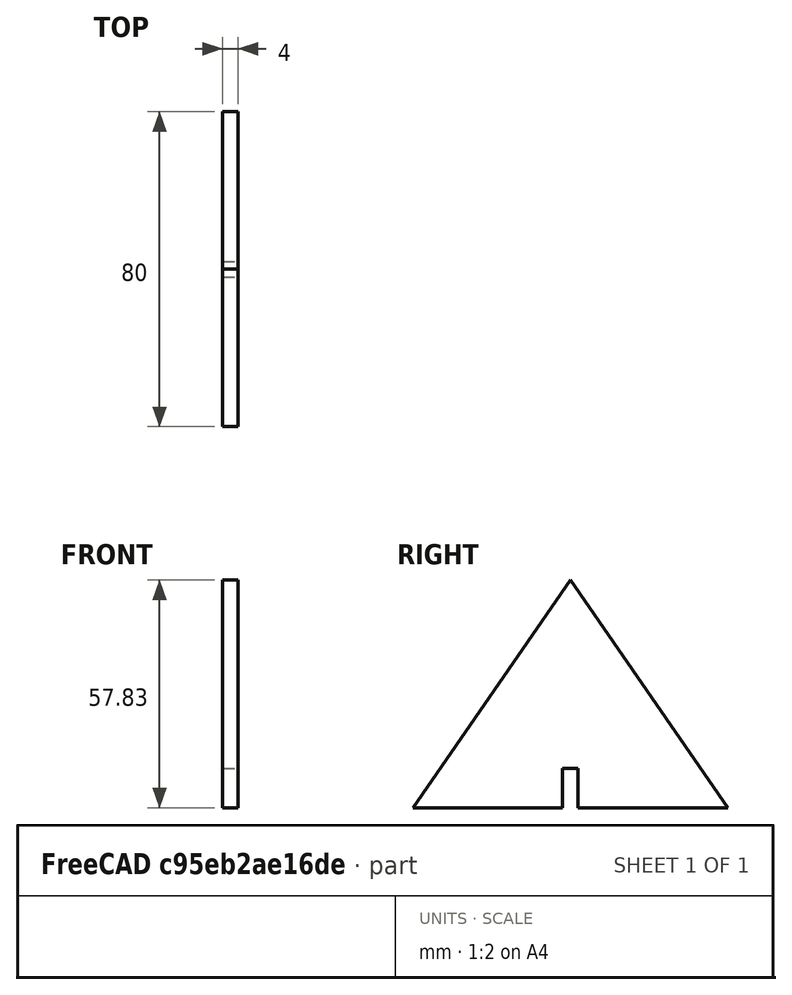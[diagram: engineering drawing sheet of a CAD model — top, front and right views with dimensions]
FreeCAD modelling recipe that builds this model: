
FCSTD DOCUMENT  (FreeCAD 0.18R16131 (Git))
Label: freccia
License: All rights reserved
LicenseURL: http://en.wikipedia.org/wiki/All_rights_reserved
objects: Sketcher::SketchObject×1, PartDesign::Pad×1, PartDesign::Body×1
note: 4 computed .brp shape members not serialized (recipe doc carries the construction recipe); baked Part::Feature solids carry a one-line shape summary decoded from their .brp

FEATURE [Sketcher::SketchObject] Sketch
  MapMode = 5
  Placement = pos=(0,0,0) rot=(0.57735,0.57735,0.57735;2.0944rad)
  Support = -> [YZ_Plane]
  sketch-geometry (7):
    g0: LineSegment StartX=0 StartY=58 StartZ=0 EndX=-40 EndY=0.173901 EndZ=0
    g1: LineSegment StartX=-40 StartY=0.173901 StartZ=0 EndX=-2 EndY=0.173901 EndZ=0
    g2: LineSegment StartX=40 StartY=0.173901 StartZ=0 EndX=0 EndY=58 EndZ=0
    g3: LineSegment StartX=2 StartY=0.173901 StartZ=0 EndX=2 EndY=10.1739 EndZ=0
    g4: LineSegment StartX=2 StartY=10.1739 StartZ=0 EndX=-2 EndY=10.1739 EndZ=0
    g5: LineSegment StartX=-2 StartY=10.1739 StartZ=0 EndX=-2 EndY=0.173901 EndZ=0
    g6: LineSegment StartX=2 StartY=0.173901 StartZ=0 EndX=40 EndY=0.173901 EndZ=0
  constraints (16):
    c: PointOnObject(g0,g-2)
    c: Coincident(g0,g1)
    c: Coincident(g6,g2)
    c: Coincident(g2,g0)
    c: Symmetric(g6,g0,g-2)
    c: DistanceX(g0,g6) = 80
    c: DistanceY(g-1,g0) = 58
    c: Coincident(g3,g4)
    c: Coincident(g4,g5)
    c: Vertical(g3)
    c: Vertical(g5)
    c: PointOnObject(g5,g1)
    c: Symmetric(g3,g4,g-2)
    c: DistanceX(g4,g4) = 4
    c: DistanceY(g3,g3) = 10
    c: Tangent(g1,g6)
FEATURE [PartDesign::Pad] Pad
  Length = 4
  Length2 = 100
  Placement = pos=(0,0,0) rot=(0.57735,0.57735,0.57735;2.0944rad)
  Profile = -> Sketch
  Type = 0
FEATURE [PartDesign::Body] Body
  Group = -> [Sketch,Pad]
  Origin = -> Origin
  Tip = -> Pad
